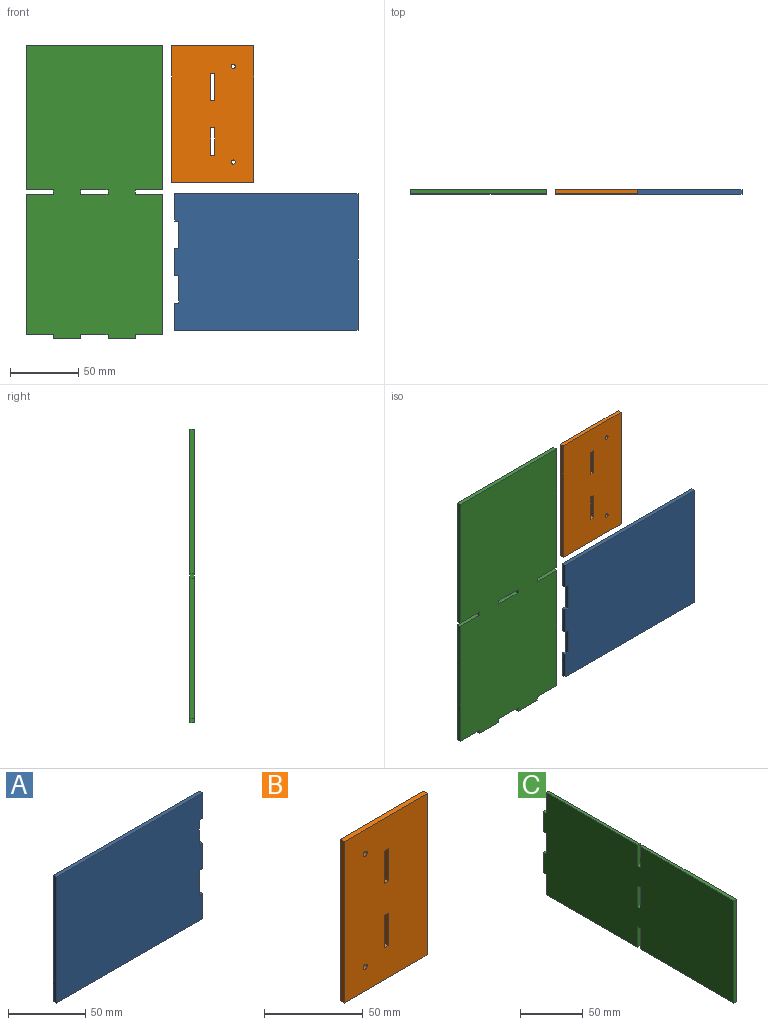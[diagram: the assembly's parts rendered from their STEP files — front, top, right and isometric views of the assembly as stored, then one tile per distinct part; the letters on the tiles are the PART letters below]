
ASSEMBLY  parts=3 mates=2
PART A: 14 faces, bbox 134x3x100 mm
  f0: plane 20x3mm, normal (1,0,0), area 60mm2, adj f2,f3,f10,f12
  f1: plane 20x3mm, normal (1,0,0), area 60mm2, adj f2,f3,f4,f9
  f2: plane 134x100mm, normal (0,-1,0), area 13280mm2, adj f0,f1,f4,f5,f6,f7,f8,f9
  f3: plane 134x100mm, normal (0,1,0), area 13280mm2, adj f0,f1,f4,f5,f6,f7,f8,f9
  f4: plane 134x3mm, normal (0,0,1), area 402mm2, adj f1,f2,f3,f5
  f5: plane 100x3mm, normal (-1,0,0), area 300mm2, adj f2,f3,f4,f6
  f6: plane 134x3mm, normal (0,0,-1), area 402mm2, adj f2,f3,f5,f7
  f7: plane 20x3mm, normal (1,0,0), area 60mm2, adj f2,f3,f6,f13
  f8: plane 20x3mm, normal (1,0,0), area 60mm2, adj f2,f3,f9,f10
  f9: plane 3x3mm, normal (0,0,-1), area 9mm2, adj f1,f2,f3,f8
  f10: plane 3x3mm, normal (0,0,1), area 9mm2, adj f0,f2,f3,f8
  f11: plane 20x3mm, normal (1,0,0), area 60mm2, adj f2,f3,f12,f13
  f12: plane 3x3mm, normal (0,0,-1), area 9mm2, adj f0,f2,f3,f11
  f13: plane 3x3mm, normal (0,0,1), area 9mm2, adj f2,f3,f7,f11
PART B: 16 faces, bbox 60x3x100 mm
  f0: plane 100x60mm, normal (0,-1,0), area 5865.9mm2, adj f2,f3,f4,f5,f6,f7,f8,f9
  f1: plane 100x60mm, normal (0,1,0), area 5865.9mm2, adj f2,f3,f4,f5,f6,f7,f8,f9
  f2: plane 60x3mm, normal (0,0,1), area 180mm2, adj f0,f1,f3,f6
  f3: plane 100x3mm, normal (-1,0,0), area 300mm2, adj f0,f1,f2,f4
  f4: plane 60x3mm, normal (0,0,-1), area 180mm2, adj f0,f1,f3,f6
  f5: cylinder r=1.5mm len=3mm, axis (0,1,0), area 28.3mm2, adj f0,f1
  f6: plane 100x3mm, normal (1,0,0), area 300mm2, adj f0,f1,f2,f4
  f7: cylinder r=1.5mm len=3mm, axis (0,1,0), area 28.3mm2, adj f0,f1
  f8: plane 20x3mm, normal (1,0,0), area 60mm2, adj f0,f1,f9,f11
  f9: plane 3x3mm, normal (0,0,-1), area 9mm2, adj f0,f1,f8,f10
  f10: plane 20x3mm, normal (-1,0,0), area 60mm2, adj f0,f1,f9,f11
  f11: plane 3x3mm, normal (0,0,1), area 9mm2, adj f0,f1,f8,f10
  f12: plane 20x3mm, normal (1,0,0), area 60mm2, adj f0,f1,f13,f15
  f13: plane 3x3mm, normal (0,0,-1), area 9mm2, adj f0,f1,f12,f14
  f14: plane 20x3mm, normal (-1,0,0), area 60mm2, adj f0,f1,f13,f15
  f15: plane 3x3mm, normal (0,0,1), area 9mm2, adj f0,f1,f12,f14
PART C: 26 faces, bbox 3x215x100 mm
  f0: plane 106x3mm, normal (0,0,1), area 318mm2, adj f2,f3,f8,f20
  f1: plane 106x3mm, normal (0,0,-1), area 318mm2, adj f2,f3,f8,f23
  f2: plane 215x100mm, normal (1,0,0), area 21140mm2, adj f0,f1,f4,f5,f6,f7,f8,f9
  f3: plane 215x100mm, normal (-1,0,0), area 21140mm2, adj f0,f1,f4,f5,f6,f7,f8,f9
  f4: plane 20x3mm, normal (0,1,0), area 60mm2, adj f2,f3,f11,f15
  f5: plane 20x3mm, normal (0,1,0), area 60mm2, adj f2,f3,f10,f13
  f6: plane 103x3mm, normal (0,0,1), area 309mm2, adj f2,f3,f12,f21
  f7: plane 103x3mm, normal (0,0,-1), area 309mm2, adj f2,f3,f14,f25
  f8: plane 100x3mm, normal (0,-1,0), area 300mm2, adj f0,f1,f2,f3
  f9: plane 20x3mm, normal (0,1,0), area 60mm2, adj f2,f3,f10,f11
  f10: plane 3x3mm, normal (0,0,-1), area 9mm2, adj f2,f3,f5,f9
  f11: plane 3x3mm, normal (0,0,1), area 9mm2, adj f2,f3,f4,f9
  f12: plane 20x3mm, normal (0,1,0), area 60mm2, adj f2,f3,f6,f13
  f13: plane 3x3mm, normal (0,0,1), area 9mm2, adj f2,f3,f5,f12
  f14: plane 20x3mm, normal (0,1,0), area 60mm2, adj f2,f3,f7,f15
  f15: plane 3x3mm, normal (0,0,-1), area 9mm2, adj f2,f3,f4,f14
  f16: plane 20x3mm, normal (0,1,0), area 60mm2, adj f2,f3,f17,f19
  f17: plane 3x3mm, normal (0,0,-1), area 9mm2, adj f2,f3,f16,f18
  f18: plane 20x3mm, normal (0,-1,0), area 60mm2, adj f2,f3,f17,f19
  f19: plane 3x3mm, normal (0,0,1), area 9mm2, adj f2,f3,f16,f18
  f20: plane 20x3mm, normal (0,1,0), area 60mm2, adj f0,f2,f3,f22
  f21: plane 20x3mm, normal (0,-1,0), area 60mm2, adj f2,f3,f6,f22
  f22: plane 3x3mm, normal (0,0,1), area 9mm2, adj f2,f3,f20,f21
  f23: plane 20x3mm, normal (0,1,0), area 60mm2, adj f1,f2,f3,f24
  f24: plane 3x3mm, normal (0,0,-1), area 9mm2, adj f2,f3,f23,f25
  f25: plane 20x3mm, normal (0,-1,0), area 60mm2, adj f2,f3,f7,f24
PLACE A rot(axis=(0,0,1),180deg) t=(-32.12,-107.61,-31.37)mm
PLACE B rot(axis=(0,0,1),180deg) t=(-5.88,-1.61,76.77)mm
PLACE C rot(axis=(-0.58,-0.58,0.58),120deg) t=(-42.49,-0.11,-37.65)mm
MATE planar A.f3 <-> C.f3  axis (0,-1,0) through (33.97,-1.61,18.63)mm
MATE planar B.f1 <-> A.f3  axis (0,-1,0) through (-5.91,-1.61,126.77)mm
